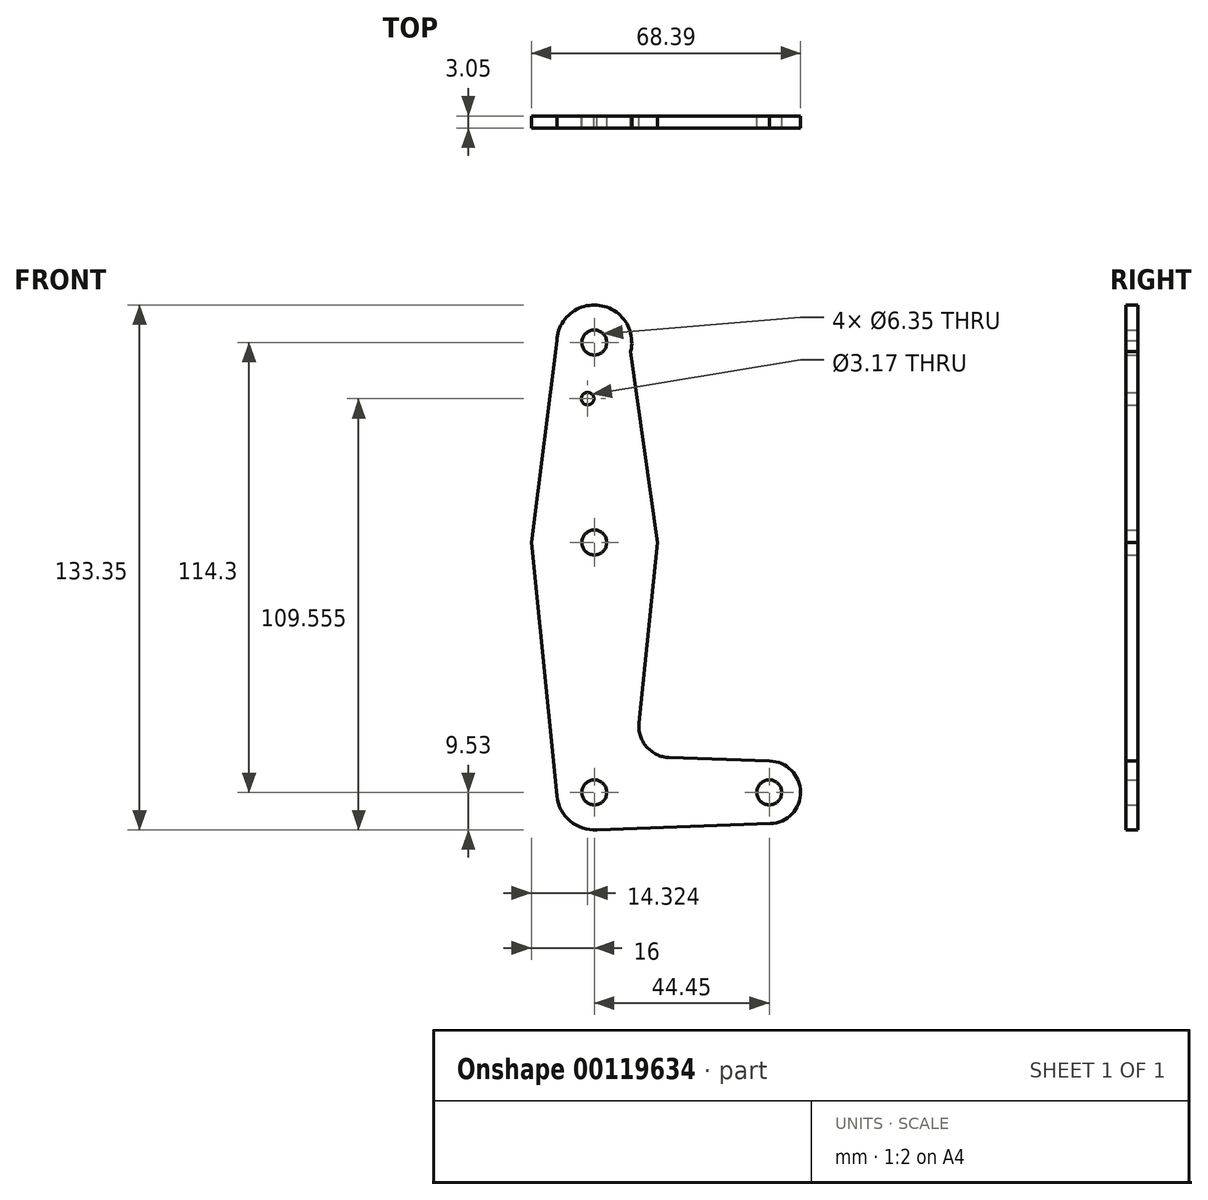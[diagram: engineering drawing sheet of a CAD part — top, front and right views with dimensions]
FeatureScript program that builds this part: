
annotation { "Feature Type Name" : "Feature", "Feature Type Description" : "" }
export const myFeature = defineFeature(function(context is Context, id is Id, definition is map)
    precondition{}
    {
        {
            var Q0;
            Q0=qCreatedBy(makeId("Front.planeOp"),FACE);
            var sketch = newSketch(context, id + "F0", { "sketchPlane" : qUnion([Q0])});
            skCircle(sketch, "E0", {"center": v(0, 0) * mm, "radius": 15.88 * mm});
            skCircle(sketch, "E1", {"center": v(0, 50.8) * mm, "radius": 9.53 * mm});
            skCircle(sketch, "E2", {"center": v(0, -63.5) * mm, "radius": 9.53 * mm});
            skCircle(sketch, "E3", {"center": v(44.45, -63.5) * mm, "radius": 7.94 * mm});
            skCircle(sketch, "E4", {"center": v(0, 50.8) * mm, "radius": 3.18 * mm});
            skCircle(sketch, "E5", {"center": v(0, 0) * mm, "radius": 3.18 * mm});
            skCircle(sketch, "E6", {"center": v(0, -63.5) * mm, "radius": 3.18 * mm});
            skCircle(sketch, "E7", {"center": v(44.45, -63.5) * mm, "radius": 3.18 * mm});
            skLineSegment(sketch, "E8", {"start": v(-9.52, 51.23) * mm, "end": v(-16, 0) * mm});
            skLineSegment(sketch, "E9", {"start": v(-16, 0) * mm, "end": v(-9.48, -64.46) * mm});
            skLineSegment(sketch, "E10", {"start": v(9.26, 48.55) * mm, "end": v(16.03, 0) * mm});
            skLineSegment(sketch, "E11", {"start": v(0, -73.03) * mm, "end": v(44.73, -71.43) * mm});
            skPoint(sketch, "E12.visualSharp", {"position": v(14.87, -55.57) * mm});
            skLineSegment(sketch, "E13", {"start": v(16.03, 0) * mm, "end": v(11.36, -45.9) * mm});
            skLineSegment(sketch, "E14", {"start": v(44.54, -55.56) * mm, "end": v(18.99, -54.65) * mm});
            skLineSegment(sketch, "E15.trimOffspring", {"start": v(0.34, -53.98) * mm, "end": v(0, -53.97) * mm});
            skPoint(sketch, "E16.visualSharp", {"position": v(10.5, -54.34) * mm});
            skArc(sketch, "E16.filletArc", {"start": v(11.36, -45.9) * mm, "mid": v(13.28, -51.93) * mm, "end": v(18.99, -54.65) * mm});
            skCircle(sketch, "E17", {"center": v(-1.68, 36.53) * mm, "radius": 1.59 * mm});
            skSolve(sketch);
        }
        {
            var Q0;
            Q0 = qSketchRegion(id + "F0", true);
            extrude(context, id + "F1", {"entities" : qUnion([Q0]), "depth" : 3.05 * mm});
        }
    });
